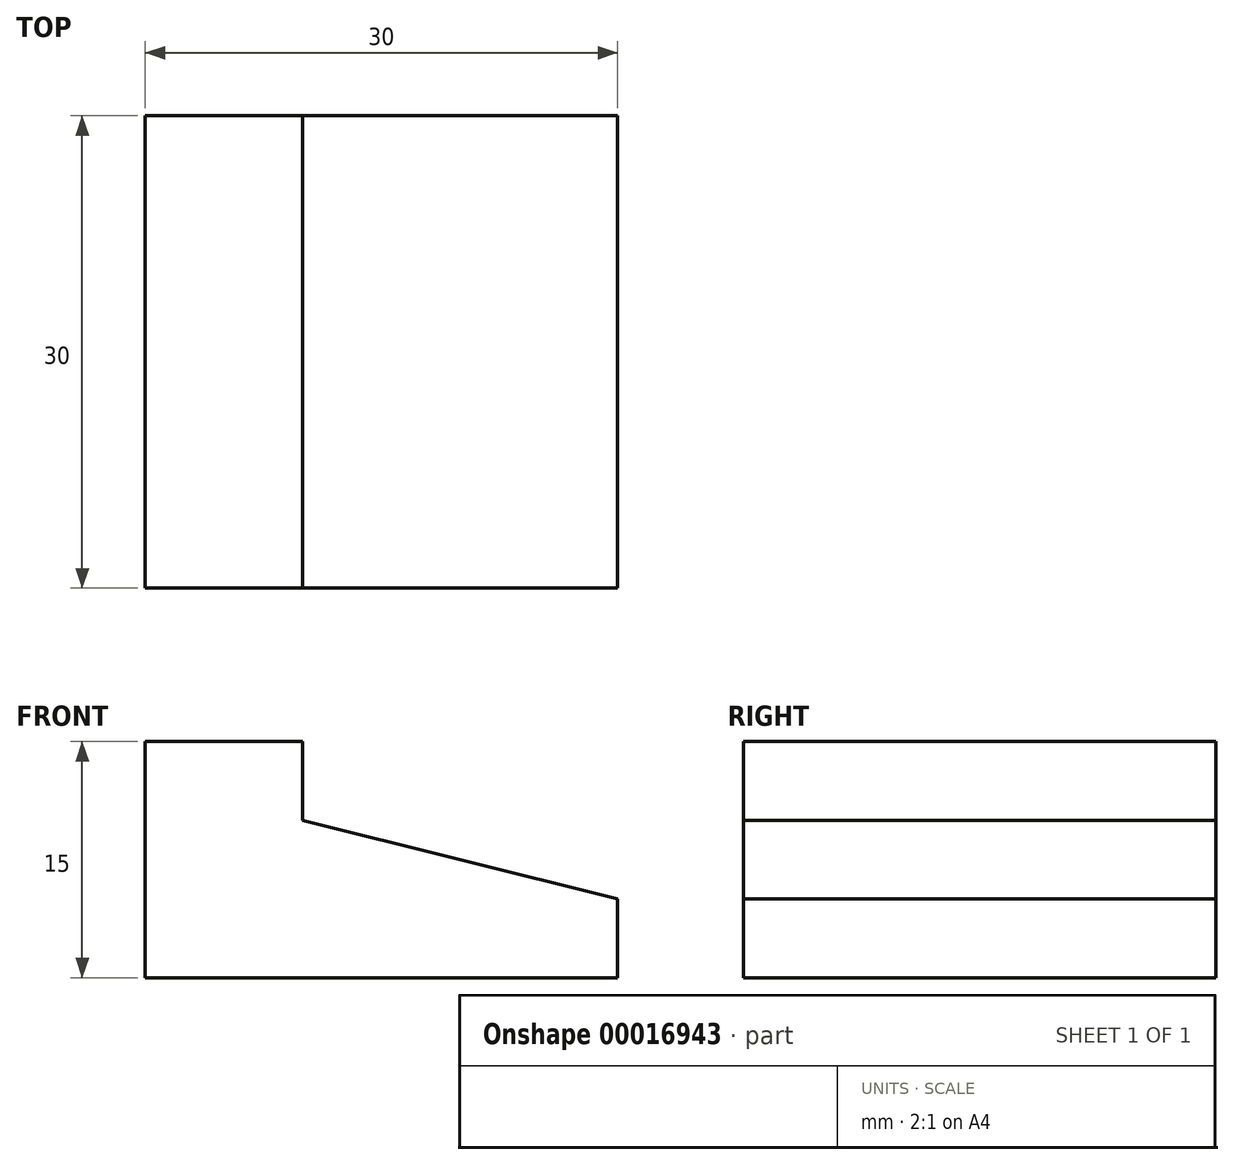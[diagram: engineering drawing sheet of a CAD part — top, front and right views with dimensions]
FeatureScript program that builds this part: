
annotation { "Feature Type Name" : "Feature", "Feature Type Description" : "" }
export const myFeature = defineFeature(function(context is Context, id is Id, definition is map)
    precondition{}
    {
        {
            var Q0;
            Q0=qCreatedBy(makeId("Front.planeOp"),FACE);
            var sketch = newSketch(context, id + "F0", { "sketchPlane" : qUnion([Q0])});
            skLineSegment(sketch, "E0", {"start": v(-24.15, 5.07) * mm, "end": v(-24.15, -9.93) * mm});
            skLineSegment(sketch, "E1", {"start": v(-24.15, -9.93) * mm, "end": v(5.85, -9.93) * mm});
            skLineSegment(sketch, "E2", {"start": v(5.85, -9.93) * mm, "end": v(5.85, -4.93) * mm});
            skLineSegment(sketch, "E3", {"start": v(5.85, -4.93) * mm, "end": v(-14.15, 0.07) * mm});
            skLineSegment(sketch, "E4", {"start": v(-14.15, 0.07) * mm, "end": v(-14.15, 5.07) * mm});
            skLineSegment(sketch, "E5", {"start": v(-14.15, 5.07) * mm, "end": v(-24.15, 5.07) * mm});
            skSolve(sketch);
        }
        {
            var Q0;
            Q0=makeQuery(id+"F0.imprint","IMPRINT",FACE,{"disambiguationData":[TD([[makeQuery(id+"F0.imprint","IMPRINT",EDGE,{"derivedFrom":sQuery(id+"F0.wireOp",EDGE,"E0")}),1.0]])]});
            extrude(context, id + "F1", {"entities" : qUnion([Q0]), "depth" : 30 * mm});
        }
    });
